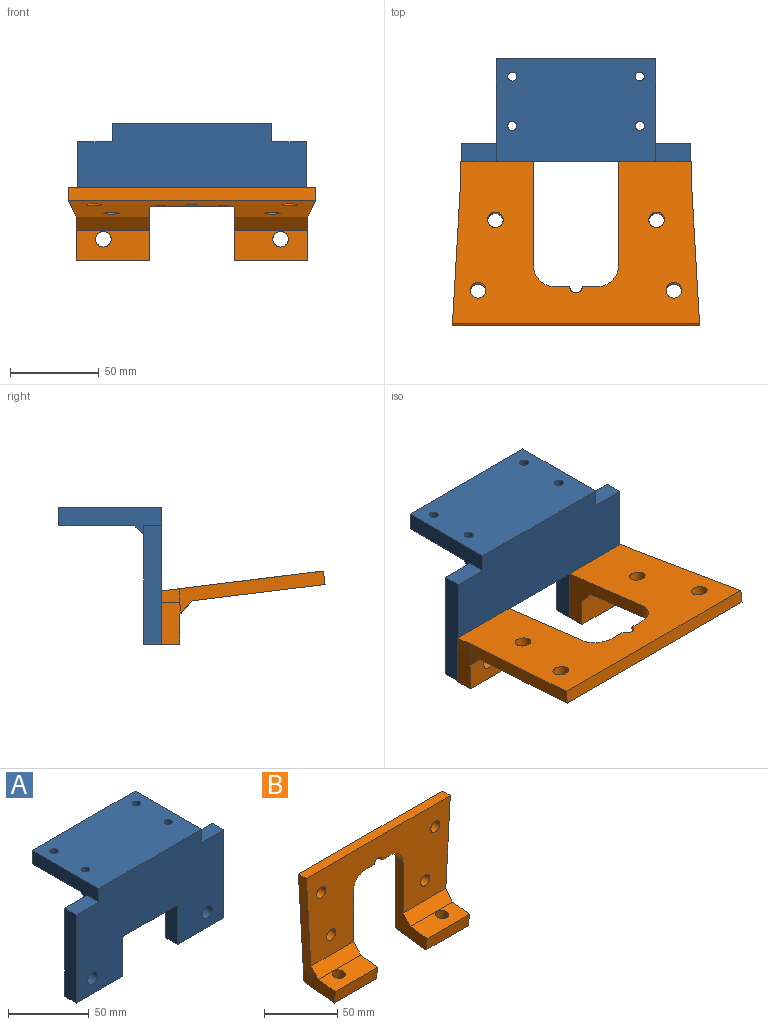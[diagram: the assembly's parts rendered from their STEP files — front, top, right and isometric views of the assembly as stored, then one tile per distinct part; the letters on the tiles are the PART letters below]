
ASSEMBLY  parts=2 mates=1
PART A: 23 faces, bbox 128.9x58x76.8 mm
  f0: plane 40.45x10.16mm, normal (0,0,-1), area 410.9mm2, adj f1,f5,f18,f19
  f1: plane 128.89x66.63mm, normal (0,1,0), area 6573.2mm2, adj f0,f4,f6,f8,f9,f14,f15,f16
  f2: plane 90x42.84mm, normal (0,0,-1), area 3774.5mm2, adj f3,f4,f6,f10,f11,f12,f13,f22
  f3: plane 90x10.16mm, normal (0,1,0), area 914.4mm2, adj f2,f4,f6,f7
  f4: plane 58x15.16mm, normal (-1,0,0), area 601.8mm2, adj f1,f2,f3,f5,f7,f9,f22
  f5: plane 128.89x76.79mm, normal (0,-1,0), area 7937.6mm2, adj f0,f4,f6,f7,f8,f9,f14,f15
  f6: plane 58x15.16mm, normal (1,0,0), area 601.8mm2, adj f1,f2,f3,f5,f7,f8,f22
  f7: plane 90x58mm, normal (0,0,1), area 5138.9mm2, adj f3,f4,f5,f6,f10,f11,f12,f13
  f8: plane 19.45x10.16mm, normal (0,0,1), area 197.6mm2, adj f1,f5,f6,f17
  f9: plane 19.45x10.16mm, normal (0,0,1), area 197.6mm2, adj f1,f4,f5,f18
  f10: cylinder r=2.54mm len=10.16mm, axis (0,0,1), area 162.1mm2, adj f2,f7
  f11: cylinder r=2.54mm len=10.16mm, axis (0,0,1), area 162.1mm2, adj f2,f7
  f12: cylinder r=2.54mm len=10.16mm, axis (0,0,1), area 162.1mm2, adj f2,f7
  f13: cylinder r=2.54mm len=10.16mm, axis (0,0,1), area 162.1mm2, adj f2,f7
  f14: cylinder r=4.45mm len=10.16mm, axis (0,-1,0), area 283.8mm2, adj f1,f5
  f15: cylinder r=4.45mm len=10.16mm, axis (0,-1,0), area 283.8mm2, adj f1,f5
  f16: plane 40.45x10.16mm, normal (0,0,-1), area 410.9mm2, adj f1,f5,f17,f20
  f17: plane 66.63x10.16mm, normal (1,0,0), area 676.9mm2, adj f1,f5,f8,f16
  f18: plane 66.63x10.16mm, normal (-1,0,0), area 676.9mm2, adj f0,f1,f5,f9
  f19: plane 30x10.16mm, normal (1,0,0), area 304.8mm2, adj f0,f1,f5,f21
  f20: plane 30x10.16mm, normal (-1,0,0), area 304.8mm2, adj f1,f5,f16,f21
  f21: plane 48x10.16mm, normal (0,0,-1), area 487.7mm2, adj f1,f5,f19,f20
  f22: plane 90x5mm, normal (0,0.71,-0.71), area 636.4mm2, adj f1,f2,f4,f6
PART B: 30 faces, bbox 139.4x31x95.6 mm
  f0: plane 40.98x10.08mm, normal (0,-0.99,-0.12), area 416.3mm2, adj f10,f22,f23,f25
  f1: plane 40.98x10.08mm, normal (0,-0.99,-0.12), area 416.3mm2, adj f2,f16,f19,f20
  f2: plane 41.02x29.78mm, normal (0,0.12,-0.99), area 1167.4mm2, adj f1,f16,f18,f20,f21,f27
  f3: plane 82.64x13.81mm, normal (-1,0,-0.06), area 648.9mm2, adj f4,f12,f18,f20,f21,f28
  f4: plane 139.39x75.64mm, normal (0,-1,0), area 7386mm2, adj f3,f5,f6,f7,f8,f9,f10,f11
  f5: cylinder r=12mm len=12mm, axis (0,1,0), area 143.6mm2, adj f4,f6,f16,f18
  f6: plane 8.5x7.62mm, normal (0,0,-1), area 64.8mm2, adj f4,f5,f7,f18
  f7: cylinder r=3.5mm len=7.62mm, axis (0,1,0), area 83.8mm2, adj f4,f6,f8,f18
  f8: plane 8.5x7.62mm, normal (0,0,-1), area 64.8mm2, adj f4,f7,f9,f18
  f9: cylinder r=12mm len=12mm, axis (0,1,0), area 143.6mm2, adj f4,f8,f10,f18
  f10: plane 62.66x31.01mm, normal (-1,0,0), area 710.6mm2, adj f0,f4,f9,f18,f22,f23,f29
  f11: plane 82.64x13.81mm, normal (1,0,-0.06), area 648.9mm2, adj f4,f12,f18,f24,f25,f29
  f12: plane 139.39x7.62mm, normal (0,0,1), area 1062.2mm2, adj f3,f4,f11,f18
  f13: cylinder r=4.45mm len=8.89mm, axis (0,1,0), area 212.8mm2, adj f4,f18
  f14: cylinder r=4.45mm len=8.89mm, axis (0,1,0), area 212.8mm2, adj f4,f18
  f15: cylinder r=4.45mm len=8.89mm, axis (0,1,0), area 212.8mm2, adj f4,f18
  f16: plane 62.66x31.01mm, normal (1,0,0), area 710.6mm2, adj f1,f2,f4,f5,f18,f19,f28
  f17: cylinder r=4.45mm len=8.89mm, axis (0,1,0), area 212.8mm2, adj f4,f18
  f18: plane 139.39x91.95mm, normal (0,1,0), area 8725.7mm2, adj f2,f3,f5,f6,f7,f8,f9,f10
  f19: plane 40.98x16.45mm, normal (0,-0.12,0.99), area 616.9mm2, adj f1,f16,f20,f27,f28
  f20: plane 24.63x12.96mm, normal (-1,0,0), area 242.1mm2, adj f1,f2,f3,f19,f21,f28
  f21: plane 11.02x7.62mm, normal (-1,-0.01,0), area 71.7mm2, adj f2,f3,f18,f20
  f22: plane 41.02x29.78mm, normal (0,0.12,-0.99), area 1167.4mm2, adj f0,f10,f18,f24,f25,f26
  f23: plane 40.98x16.45mm, normal (0,-0.12,0.99), area 616.9mm2, adj f0,f10,f25,f26,f29
  f24: plane 11.02x7.62mm, normal (1,-0.01,0), area 71.7mm2, adj f11,f18,f22,f25
  f25: plane 24.63x12.96mm, normal (1,0,0), area 242.1mm2, adj f0,f11,f22,f23,f24,f29
  f26: cylinder r=4.45mm len=11.17mm, axis (0,-0.12,0.99), area 283.8mm2, adj f22,f23
  f27: cylinder r=4.45mm len=11.17mm, axis (0,-0.12,0.99), area 283.8mm2, adj f2,f19
  f28: plane 41.38x7.85mm, normal (0,-0.75,0.66), area 431.5mm2, adj f3,f4,f16,f19,f20
  f29: plane 41.38x7.85mm, normal (0,-0.75,0.66), area 431.5mm2, adj f4,f10,f11,f23,f25
PLACE A t=(23.02,25.59,23.51)mm
PLACE B rot(axis=(1,0,0),83deg) t=(-280.47,-71.02,-7.82)mm
MATE parallel B.f26 <-> A.f15  axis (0,1,0) through (57.43,-27.86,-31.33)mm
